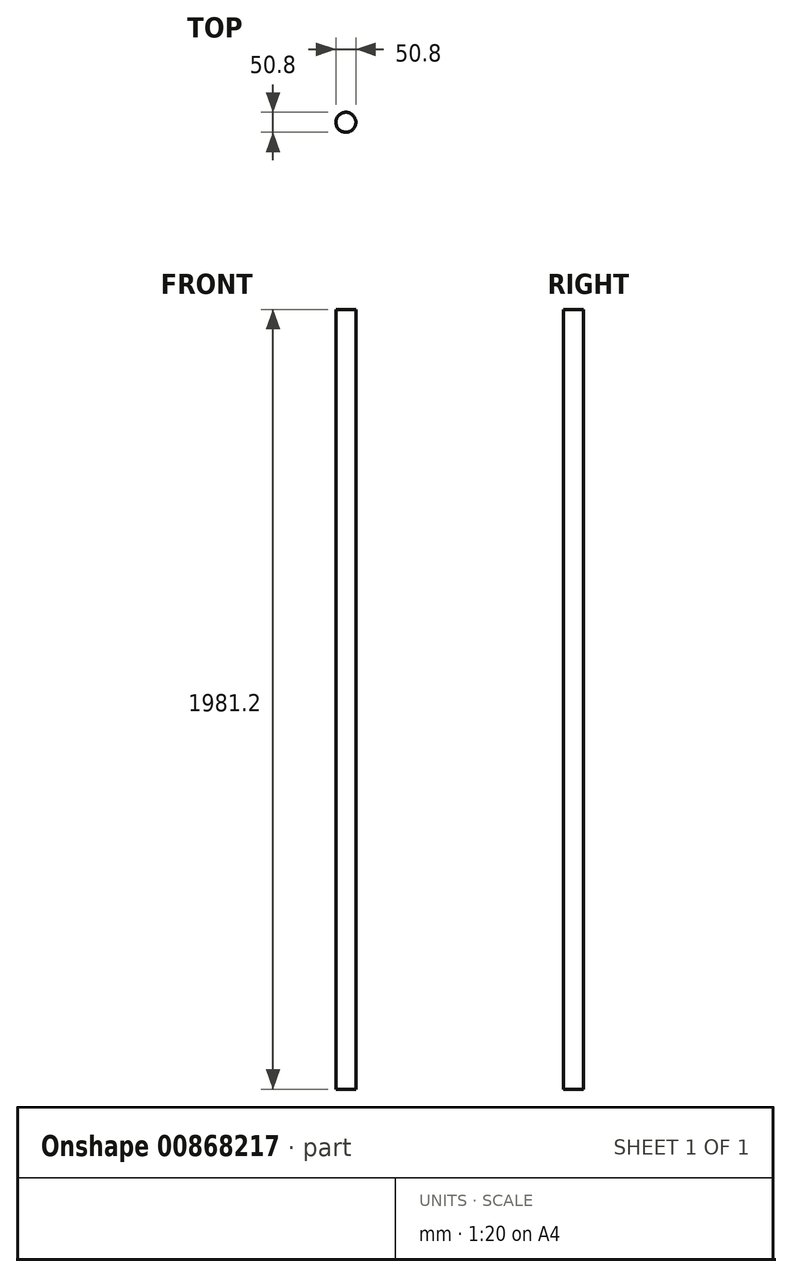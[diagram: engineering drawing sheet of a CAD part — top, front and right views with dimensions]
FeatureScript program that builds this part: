
annotation { "Feature Type Name" : "Feature", "Feature Type Description" : "" }
export const myFeature = defineFeature(function(context is Context, id is Id, definition is map)
    precondition{}
    {
        {
            var Q0;
            Q0=qCreatedBy(makeId("Top.planeOp"),FACE);
            var sketch = newSketch(context, id + "F0", { "sketchPlane" : qUnion([Q0])});
            skCircle(sketch, "E0", {"center": v(0, 0) * mm, "radius": 25.4 * mm});
            skSolve(sketch);
        }
        {
            var Q0;
            Q0 = qSketchRegion(id + "F0", true);
            extrude(context, id + "F1", {"entities" : qUnion([Q0]), "depth" : 1981.2 * mm, "offsetDistance" : 25.4 * mm});
        }
    });
